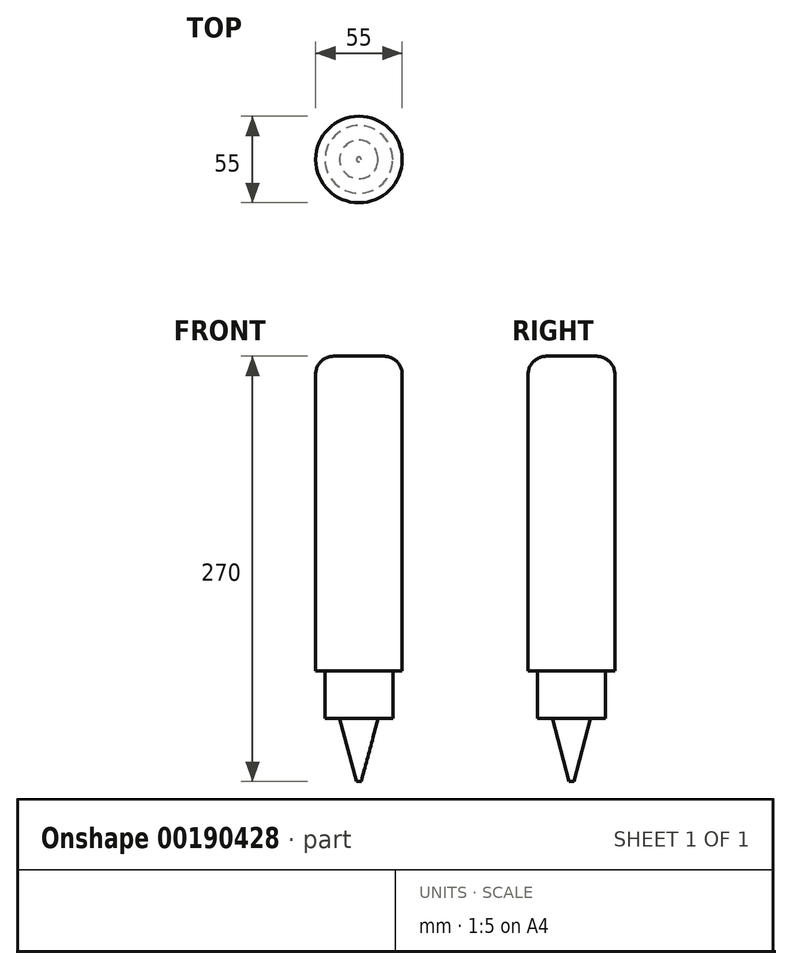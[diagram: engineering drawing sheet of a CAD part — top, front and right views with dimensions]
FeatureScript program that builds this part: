
annotation { "Feature Type Name" : "Feature", "Feature Type Description" : "" }
export const myFeature = defineFeature(function(context is Context, id is Id, definition is map)
    precondition{}
    {
        {
            var Q0;
            Q0=qCreatedBy(makeId("Top.planeOp"),FACE);
            var sketch = newSketch(context, id + "F0", { "sketchPlane" : qUnion([Q0])});
            skCircle(sketch, "E0", {"center": v(22.42, 24.54) * mm, "radius": 27.5 * mm});
            skCircle(sketch, "E1", {"center": v(22.42, 24.54) * mm, "radius": 21.5 * mm});
            skCircle(sketch, "E2", {"center": v(22.42, 24.54) * mm, "radius": 1.5 * mm});
            skSolve(sketch);
        }
        {
            var Q0;
            Q0 = qSketchRegion(id + "F0", true);
            var Q1;
            Q1=makeQuery(id+"F0.imprint","IMPRINT",FACE,{"disambiguationData":[TD([[makeQuery(id+"F0.imprint","IMPRINT",EDGE,{"derivedFrom":sQuery(id+"F0.wireOp",EDGE,"E1")}),1.0]])]});
            var Q2;
            Q2=makeQuery(id+"F0.imprint","IMPRINT",FACE,{"disambiguationData":[TD([[makeQuery(id+"F0.imprint","IMPRINT",EDGE,{"derivedFrom":sQuery(id+"F0.wireOp",EDGE,"E2")}),1.0]])]});
            extrude(context, id + "F1", {"entities" : qUnion([Q0, Q1, Q2]), "depth" : 270 * mm, "hasSecondDirection" : true, "secondDirectionOppositeDirection" : false, "secondDirectionDepth" : 70 * mm});
        }
        {
            var Q0;
            Q0=makeQuery(id+"F0.imprint","IMPRINT",FACE,{"disambiguationData":[TD([[makeQuery(id+"F0.imprint","IMPRINT",EDGE,{"derivedFrom":sQuery(id+"F0.wireOp",EDGE,"E1")}),1.0]])]});
            var Q1;
            Q1=makeQuery(id+"F0.imprint","IMPRINT",FACE,{"disambiguationData":[TD([[makeQuery(id+"F0.imprint","IMPRINT",EDGE,{"derivedFrom":sQuery(id+"F0.wireOp",EDGE,"E2")}),1.0]])]});
            extrude(context, id + "F2", {"entities" : qUnion([Q0, Q1]), "operationType" : NewBodyOperationType.ADD, "depth" : 70 * mm, "hasSecondDirection" : true, "secondDirectionOppositeDirection" : false, "secondDirectionDepth" : 40 * mm});
        }
        {
            var Q0;
            Q0=makeQuery(id+"F0.imprint","IMPRINT",FACE,{"disambiguationData":[TD([[makeQuery(id+"F0.imprint","IMPRINT",EDGE,{"derivedFrom":sQuery(id+"F0.wireOp",EDGE,"E2")}),1.0]])]});
            extrude(context, id + "F3", {"entities" : qUnion([Q0]), "operationType" : NewBodyOperationType.ADD, "depth" : 40 * mm, "hasDraft" : true, "draftAngle" : 15 * degree});
        }
        {
            var Q0;
            Q0=makeQuery(id+"F1.opExtrude","CAP_EDGE",EDGE,{"disambiguationData":[OSD([sQuery(id+"F0.wireOp",EDGE,"E0")])],"isStart":false});
            fillet(context, id + "F4", {"entities" : qUnion([Q0]), "radius" : 11.35 * mm, "tangentPropagation" : true, "allowEdgeOverflow" : false});
        }
    });
